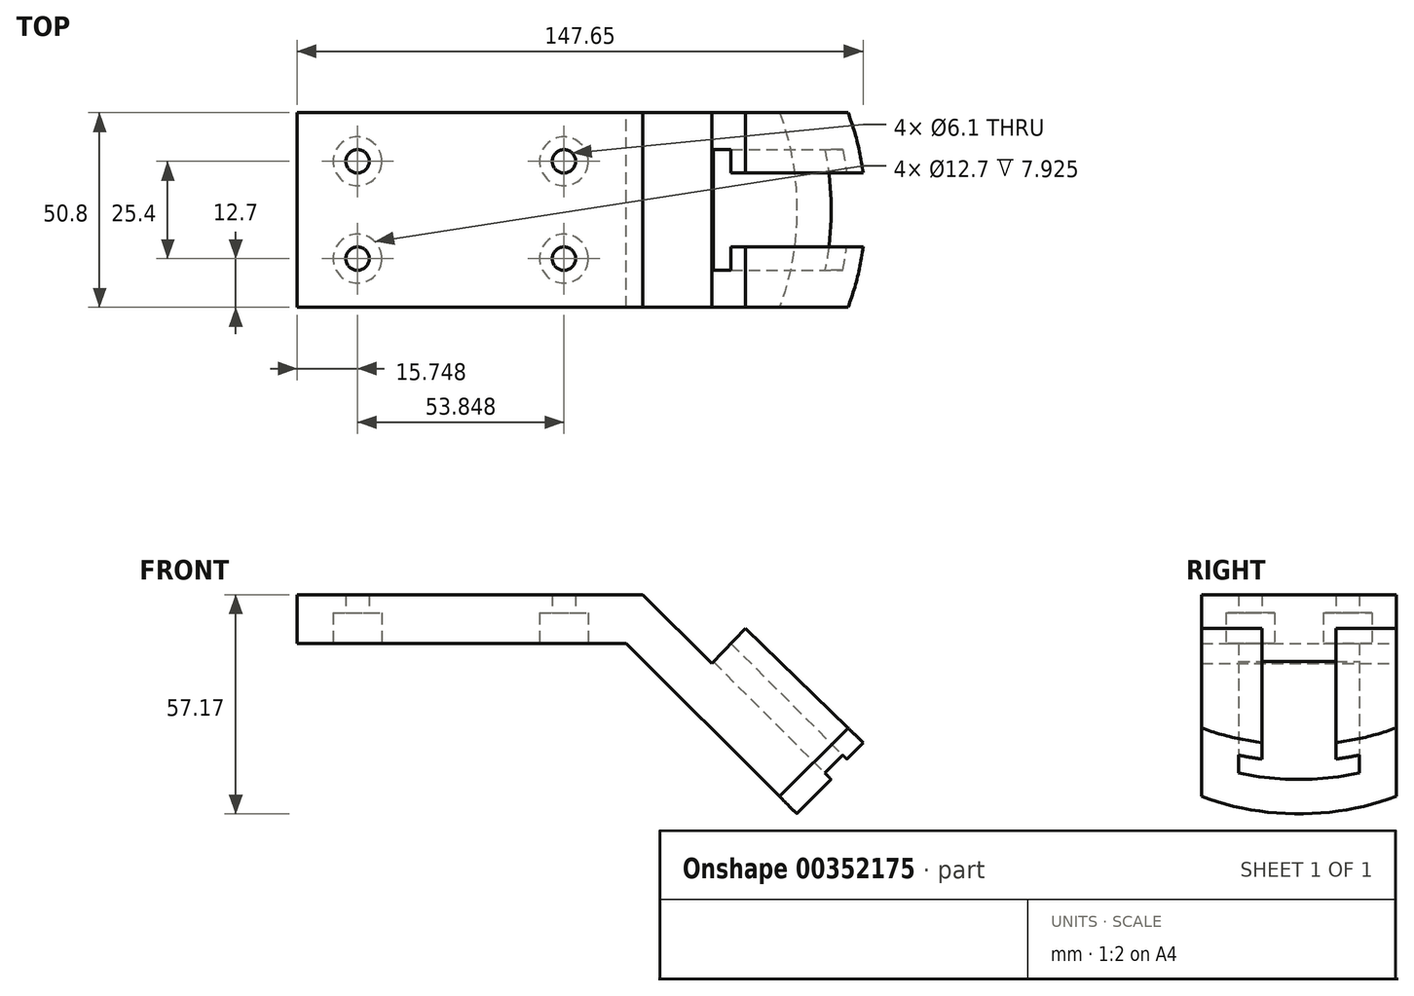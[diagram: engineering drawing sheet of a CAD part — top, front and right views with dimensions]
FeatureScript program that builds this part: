
annotation { "Feature Type Name" : "Feature", "Feature Type Description" : "" }
export const myFeature = defineFeature(function(context is Context, id is Id, definition is map)
    precondition{}
    {
        {
            var Q0;
            Q0=qCreatedBy(makeId("Front.planeOp"),FACE);
            var sketch = newSketch(context, id + "F0", { "sketchPlane" : qUnion([Q0])});
            skLineSegment(sketch, "E0", {"start": v(0, 0) * mm, "end": v(85.85, 0) * mm});
            skLineSegment(sketch, "E1", {"start": v(85.85, 0) * mm, "end": v(130.32, -44.47) * mm});
            skLineSegment(sketch, "E2", {"start": v(90.16, 12.7) * mm, "end": v(0, 12.7) * mm});
            skLineSegment(sketch, "E3", {"start": v(0, 12.7) * mm, "end": v(0, 0) * mm});
            skLineSegment(sketch, "E4", {"start": v(90.16, 12.7) * mm, "end": v(98, 12.7) * mm, "construction": true});
            skLineSegment(sketch, "E5", {"start": v(148.28, -26.5) * mm, "end": v(116.96, 3.86) * mm});
            skLineSegment(sketch, "E6", {"start": v(116.96, 3.86) * mm, "end": v(108.12, -5.26) * mm});
            skLineSegment(sketch, "E7", {"start": v(108.12, -5.26) * mm, "end": v(90.16, 12.7) * mm});
            skLineSegment(sketch, "E8", {"start": v(148.28, -26.5) * mm, "end": v(130.32, -44.47) * mm});
            skSolve(sketch);
        }
        {
            var Q0;
            Q0=makeQuery(id+"F0.imprint","IMPRINT",FACE,{"disambiguationData":[TD([[makeQuery(id+"F0.imprint","IMPRINT",EDGE,{"derivedFrom":sQuery(id+"F0.wireOp",EDGE,"E0")}),1.0]])]});
            extrude(context, id + "F1", {"entities" : qUnion([Q0]), "depth" : 50.8 * mm});
        }
        {
            var Q0;
            Q0=makeQuery(id+"F1.opExtrude","SWEPT_FACE",FACE,{"disambiguationData":[OSD([sQuery(id+"F0.wireOp",EDGE,"E0")])]});
            var sketch = newSketch(context, id + "F2", { "sketchPlane" : qUnion([Q0])});
            skLineSegment(sketch, "E9", {"start": v(0, 25.4) * mm, "end": v(85.85, 25.4) * mm, "construction": true});
            skCircle(sketch, "E10", {"center": v(15.75, 38.1) * mm, "radius": 3.96 * mm});
            skCircle(sketch, "E11", {"center": v(69.6, 38.1) * mm, "radius": 3.96 * mm});
            skCircle(sketch, "E12.MirrorC", {"center": v(15.75, 12.7) * mm, "radius": 3.96 * mm});
            skCircle(sketch, "E13.MirrorC", {"center": v(69.6, 12.7) * mm, "radius": 3.96 * mm});
            skSolve(sketch);
        }
        {
            var Q0;
            Q0=sQuery(id+"F2.wireOp",VERTEX,"E10.center");
            var Q1;
            Q1=sQuery(id+"F2.wireOp",VERTEX,"E12.MirrorC.center");
            var Q2;
            Q2=sQuery(id+"F2.wireOp",VERTEX,"E13.MirrorC.center");
            var Q3;
            Q3=sQuery(id+"F2.wireOp",VERTEX,"E11.center");
            var Q4;
            Q4=makeQuery(id+"F1.opExtrude","SWEPT_BODY",BODY,{"disambiguationData":[OSD([sQuery(id+"F0.wireOp",EDGE,"E0"),sQuery(id+"F0.wireOp",EDGE,"E1"),sQuery(id+"F0.wireOp",EDGE,"E2"),sQuery(id+"F0.wireOp",EDGE,"E3"),sQuery(id+"F0.wireOp",EDGE,"E5"),sQuery(id+"F0.wireOp",EDGE,"E6"),sQuery(id+"F0.wireOp",EDGE,"E7"),sQuery(id+"F0.wireOp",EDGE,"E8")])]});
            hole(context, id + "F3", {"style" : HoleStyle.C_BORE, "endStyle" : HoleEndStyle.THROUGH, "holeDiameter" : 6.1 * mm, "cBoreDiameter" : 12.7 * mm, "cBoreDepth" : 7.92 * mm, "isTappedThrough" : true, "tappedDepth" : 12.7 * mm, "tapClearance" : 3, "startFromSketch" : true, "locations" : qUnion([Q0, Q1, Q2, Q3]), "scope" : qUnion([Q4])});
        }
        {
            var Q0;
            Q0=makeQuery(id+"F1.opExtrude","SWEPT_FACE",FACE,{"disambiguationData":[OSD([sQuery(id+"F0.wireOp",EDGE,"E8")])]});
            var sketch = newSketch(context, id + "F4", { "sketchPlane" : qUnion([Q0])});
            skLineSegment(sketch, "E14", {"start": v(-25.4, 86.1) * mm, "end": v(-25.4, 60.7) * mm, "construction": true});
            skLineSegment(sketch, "E15", {"start": v(-35.05, 86.1) * mm, "end": v(-35.05, 80.01) * mm});
            skLineSegment(sketch, "E16", {"start": v(-35.05, 80.01) * mm, "end": v(-41.15, 80.01) * mm});
            skLineSegment(sketch, "E17", {"start": v(-41.15, 80.01) * mm, "end": v(-41.15, 73.4) * mm});
            skLineSegment(sketch, "E18", {"start": v(-41.15, 73.4) * mm, "end": v(-25.4, 73.4) * mm});
            skLineSegment(sketch, "E19.MirrorCS", {"start": v(-9.65, 73.4) * mm, "end": v(-25.4, 73.4) * mm});
            skLineSegment(sketch, "E20.MirrorCS", {"start": v(-15.75, 80.01) * mm, "end": v(-9.65, 80.01) * mm});
            skLineSegment(sketch, "E21.MirrorCS", {"start": v(-15.75, 86.1) * mm, "end": v(-15.75, 80.01) * mm});
            skLineSegment(sketch, "E22.MirrorCS", {"start": v(-9.65, 80.01) * mm, "end": v(-9.65, 73.4) * mm});
            skLineSegment(sketch, "E23", {"start": v(-35.05, 86.1) * mm, "end": v(-15.75, 86.1) * mm});
            skSolve(sketch);
        }
        {
            var Q0;
            Q0=makeQuery(id+"F4.imprint","IMPRINT",FACE,{"disambiguationData":[TD([[makeQuery(id+"F4.imprint","IMPRINT",EDGE,{"derivedFrom":sQuery(id+"F4.wireOp",EDGE,"E15")}),1.0]])]});
            extrude(context, id + "F5", {"entities" : qUnion([Q0]), "operationType" : NewBodyOperationType.REMOVE, "endBound" : BoundingType.THROUGH_ALL, "oppositeDirection" : true, "depth" : 25.4 * mm});
        }
        {
            var Q0;
            Q0=makeQuery(id+"F1.opExtrude","SWEPT_FACE",FACE,{"disambiguationData":[OSD([sQuery(id+"F0.wireOp",EDGE,"E1")])]});
            var sketch = newSketch(context, id + "F6", { "sketchPlane" : qUnion([Q0])});
            skArc(sketch, "E24", {"start": v(0, -117.22) * mm, "mid": v(25.4, -123.6) * mm, "end": v(50.8, -117.22) * mm});
            skLineSegment(sketch, "E25", {"start": v(25.4, -123.6) * mm, "end": v(25.4, -60.7) * mm, "construction": true});
            skSolve(sketch);
        }
        {
            var Q0;
            {var subQ0=sQuery(id+"F6.wireOp",EDGE,"E24");var subQ1=sQuery(id+"F0.wireOp",EDGE,"E1");var subQ2=makeQuery(id+"F1.opExtrude","CAP_EDGE",EDGE,{"disambiguationData":[OSD([subQ1])],"isStart":true});var subQ3=makeQuery(id+"F6.imprint","INTERSECT",VERTEX,{"derivedFrom":[subQ2,subQ0]});Q0=makeQuery(id+"F6.imprint","IMPRINT",FACE,{"disambiguationData":[TD([[makeQuery(id+"F6.imprint","IMPRINT",EDGE,{"disambiguationData":[TD([[subQ3,-1.0]])],"derivedFrom":subQ0}),-1.0]])]});}
            var Q1;
            {var subQ0=sQuery(id+"F6.wireOp",EDGE,"E24");var subQ1=sQuery(id+"F0.wireOp",EDGE,"E1");var subQ2=makeQuery(id+"F1.opExtrude","CAP_EDGE",EDGE,{"disambiguationData":[OSD([subQ1])],"isStart":false});var subQ3=makeQuery(id+"F6.imprint","INTERSECT",VERTEX,{"derivedFrom":[subQ2,subQ0]});Q1=makeQuery(id+"F6.imprint","IMPRINT",FACE,{"disambiguationData":[TD([[makeQuery(id+"F6.imprint","IMPRINT",EDGE,{"disambiguationData":[TD([[subQ3,1.0]])],"derivedFrom":subQ0}),-1.0]])]});}
            extrude(context, id + "F7", {"entities" : qUnion([Q0, Q1]), "operationType" : NewBodyOperationType.REMOVE, "endBound" : BoundingType.THROUGH_ALL, "oppositeDirection" : true, "depth" : 25.4 * mm});
        }
    });
